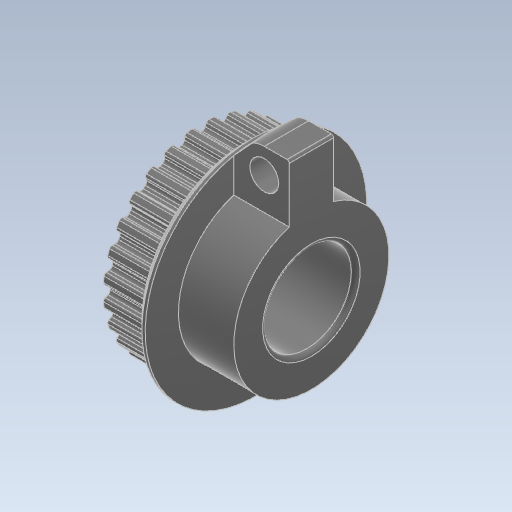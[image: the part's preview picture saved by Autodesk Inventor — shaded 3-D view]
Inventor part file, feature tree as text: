
AUTODESK INVENTOR PART (.ipt)
format: ipt  version: 2024 (Build 280153000, 153)  size: 654,848 bytes
history: native  units: mm
features: other x4, revolve x3, sketch x1, extrude x1, fillet x1
ambient origin geometry x8: Origin, YZ Plane, XZ Plane, XY Plane, X Axis, Y Axis, Z Axis, Center Point
bodies: Solid1 (feature_tree)
feature tree (10):
  other  "brideye_elbowUnit_pully-origin.ipt"
  sketch  "スケッチ3"
  revolve  "回転3"
  revolve  "回転4"
  extrude  "押し出し1"  Depth=14.0mm
  revolve  "回転5"
  fillet  "フィレット1"  [1 undecoded]
  other  "Solid1::brideye_elbowUnit_pully-origin.ipt"
  other  "TaggingFeature2"
  other  "スケッチ3_1"
note: 1 required parameter value undecoded (feature->parameter linkage not recoverable at this tier; creation-order binding heuristic only, values carry confidence <= 0.55)
